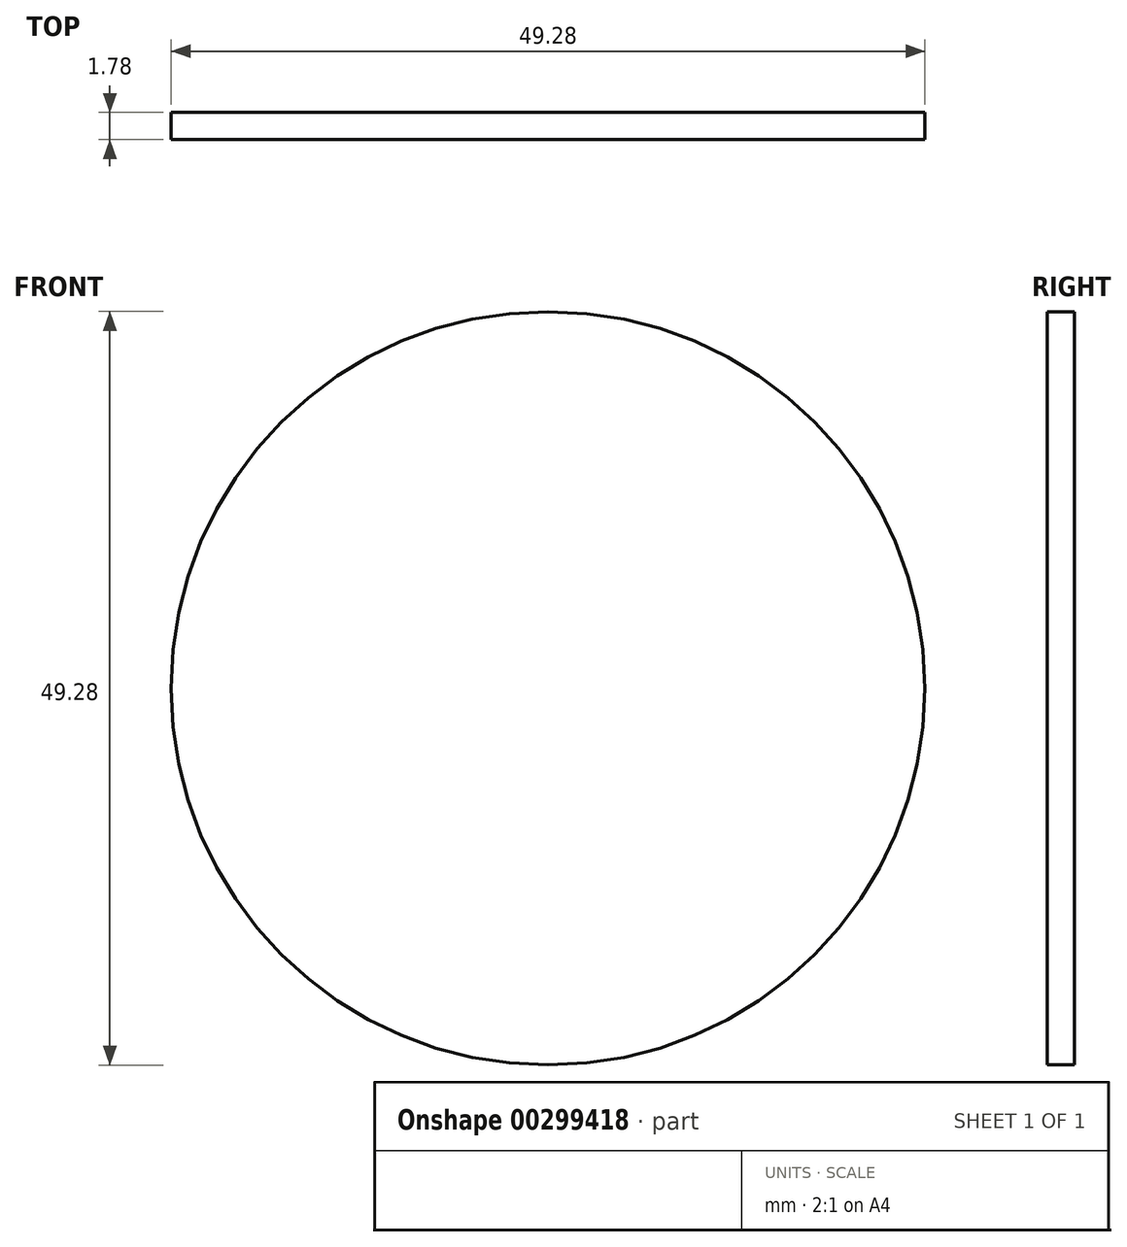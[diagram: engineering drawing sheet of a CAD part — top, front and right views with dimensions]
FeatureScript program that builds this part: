
annotation { "Feature Type Name" : "Feature", "Feature Type Description" : "" }
export const myFeature = defineFeature(function(context is Context, id is Id, definition is map)
    precondition{}
    {
        {
            var Q0;
            Q0=qCreatedBy(makeId("Front.planeOp"),FACE);
            var sketch = newSketch(context, id + "F0", { "sketchPlane" : qUnion([Q0])});
            skCircle(sketch, "E0", {"center": v(8.06, 12.95) * mm, "radius": 24.64 * mm});
            skSolve(sketch);
        }
        {
            var Q0;
            Q0 = qSketchRegion(id + "F0", true);
            extrude(context, id + "F1", {"entities" : qUnion([Q0]), "depth" : 1.78 * mm});
        }
    });
